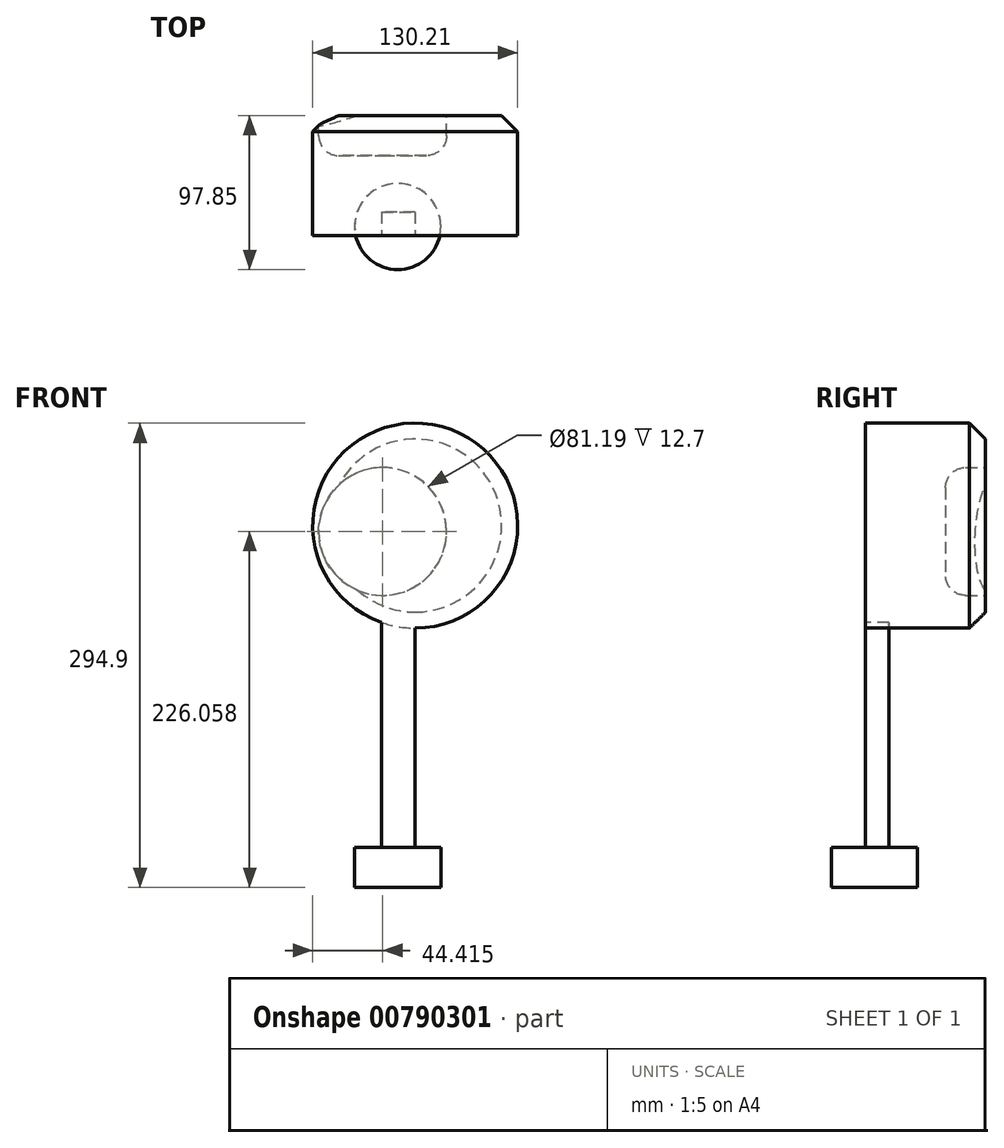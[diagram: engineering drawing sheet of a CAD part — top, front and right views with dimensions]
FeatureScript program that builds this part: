
annotation { "Feature Type Name" : "Feature", "Feature Type Description" : "" }
export const myFeature = defineFeature(function(context is Context, id is Id, definition is map)
    precondition{}
    {
        {
            var Q0;
            Q0=qCreatedBy(makeId("Top.planeOp"),FACE);
            var sketch = newSketch(context, id + "F0", { "sketchPlane" : qUnion([Q0])});
            skCircle(sketch, "E0", {"center": v(-20.41, 28.93) * mm, "radius": 27.35 * mm});
            skSolve(sketch);
        }
        {
            var Q0;
            Q0 = qSketchRegion(id + "F0", true);
            extrude(context, id + "F1", {"entities" : qUnion([Q0]), "depth" : 25.4 * mm, "offsetDistance" : 25.4 * mm});
        }
        {
            var Q0;
            Q0=makeQuery(id+"F1.opExtrude","CAP_FACE",FACE,{"disambiguationData":[OSD([sQuery(id+"F0.wireOp",EDGE,"E0")])],"isStart":false});
            var sketch = newSketch(context, id + "F2", { "sketchPlane" : qUnion([Q0])});
            skLineSegment(sketch, "E1.bottom", {"start": v(-30.82, 38.18) * mm, "end": v(-9.33, 38.18) * mm});
            skLineSegment(sketch, "E1.top", {"start": v(-30.82, 23.23) * mm, "end": v(-9.33, 23.23) * mm});
            skLineSegment(sketch, "E1.left", {"start": v(-30.82, 38.18) * mm, "end": v(-30.82, 23.23) * mm});
            skLineSegment(sketch, "E1.right", {"start": v(-9.33, 38.18) * mm, "end": v(-9.33, 23.23) * mm});
            skSolve(sketch);
        }
        {
            var Q0;
            Q0 = qSketchRegion(id + "F2", true);
            extrude(context, id + "F3", {"entities" : qUnion([Q0]), "operationType" : NewBodyOperationType.ADD, "depth" : 228.6 * mm, "offsetDistance" : 25.4 * mm});
        }
        {
            var Q0;
            Q0=makeQuery(id+"F3.opExtrude","SWEPT_FACE",FACE,{"disambiguationData":[OSD([sQuery(id+"F2.wireOp",EDGE,"E1.top")])]});
            var sketch = newSketch(context, id + "F4", { "sketchPlane" : qUnion([Q0])});
            skCircle(sketch, "E2", {"center": v(-9.33, 229.8) * mm, "radius": 65.1 * mm});
            skSolve(sketch);
        }
        {
            var Q0;
            Q0 = qSketchRegion(id + "F4", true);
            extrude(context, id + "F5", {"entities" : qUnion([Q0]), "operationType" : NewBodyOperationType.ADD, "oppositeDirection" : true, "depth" : 76.2 * mm, "offsetDistance" : 25.4 * mm});
        }
        {
            var Q0;
            Q0=makeQuery(id+"F5.opExtrude","CAP_FACE",FACE,{"disambiguationData":[OSD([sQuery(id+"F4.wireOp",EDGE,"E2")])],"isStart":false});
            var sketch = newSketch(context, id + "F6", { "sketchPlane" : qUnion([Q0])});
            skCircle(sketch, "E3", {"center": v(30.02, 226.06) * mm, "radius": 40.6 * mm});
            skSolve(sketch);
        }
        {
            var Q0;
            Q0 = qSketchRegion(id + "F6", true);
            extrude(context, id + "F7", {"entities" : qUnion([Q0]), "operationType" : NewBodyOperationType.REMOVE, "oppositeDirection" : true, "depth" : 25.4 * mm, "offsetDistance" : 25.4 * mm});
        }
        {
            var Q0;
            Q0=makeQuery(id+"F7.boolean.opBoolean","COPY",EDGE,{"derivedFrom":makeQuery(id+"F7.opExtrude","CAP_EDGE",EDGE,{"disambiguationData":[OSD([sQuery(id+"F6.wireOp",EDGE,"E3")])],"isStart":false})});
            fillet(context, id + "F8", {"entities" : qUnion([Q0]), "radius" : 12.7 * mm, "tangentPropagation" : true, "allowEdgeOverflow" : false});
        }
        {
            var Q0;
            Q0=makeQuery(id+"F5.opExtrude","CAP_EDGE",EDGE,{"disambiguationData":[OSD([sQuery(id+"F4.wireOp",EDGE,"E2")])],"isStart":false});
            chamfer(context, id + "F9", {"entities" : qUnion([Q0]), "width" : 10.16 * mm, "tangentPropagation" : true});
        }
    });
